# Revit family: GALAD Эконом GR LED
name_source: partatom
category: Осветительные приборы
revit_build: Autodesk Revit 2018 (Build: 20180423_1000(x64)
units: mm (PartAtom-declared; Revit-internal decimal feet)

## family parameters
Источник света = Да
Общий = Нет
Основа = Грань
При загрузке вырезать с полостями = Да
Размер круглого соединителя = Использовать диаметр
Тип детали = Нормальный
Точка расчета площади = Нет

## types (1)
- GALAD Эконом LED-35/У/П/4000/6060 GR
    ADSK_Версия Revit = 2018
    ADSK_Версия семейства = 1.01
    ADSK_Единица измерения = шт.
    ADSK_Завод-изготовитель = АО «КАДОШКИНСКИЙ ЭЛЕКТРОТЕХНИЧЕСКИЙ ЗАВОД»
    ADSK_Классификация нагрузок = Освещение
    ADSK_Код изделия = 17877
    ADSK_Количество = 1
    ADSK_Количество фаз = 1
    ADSK_Количество фаз числовое = 1
    ADSK_Коэффициент мощности = 0.95
    ADSK_Марка = GALAD Эконом LED-35/У/П/4000/6060 GR
    ADSK_Масса = 3.4
    ADSK_Наименование = GALAD Эконом LED-35/У/П/4000/6060 GR
    ADSK_Наименование краткое = GALAD Эконом LED-35/У/П/4000/6060 GR
    ADSK_Напряжение = 230 В
    ADSK_Номинальная мощность = 35 Вт
    ADSK_Обозначение = ГОСТ 15150-69
    ADSK_Полная мощность = 37 В·А
    ADSK_Размер_Высота = 45 мм
    ADSK_Размер_Длина = 588 мм
    ADSK_Размер_Ширина = 588 мм
    ADSK_Ток = 0 А
    ADSK_Энергоэффективность = 103 лм/Вт
    IP = 20
    URL = https://galad.ru
    Блок аварийного питания = Нет
    Бортик внешней рамки = 0 мм
    Видимая форма излучения при визуализации = Нет
    Возможный угол наклона = 0
    Высота бортика внешнего = 4 мм
    Габаритная яркость в зоне ограничения яркости = 0
    Группа модели = GALAD Эконом LED
    Диапазон цветовой температуры = 3985±275
    Излучение по длине прямоугольника = 588 мм
    Излучение по ширине прямоугольника = 588 мм
    Класс защиты от поражения электрическим током = 1
    Класс светораспределения = П
    Климатическая зона = УХЛ4
    Климатическое исполнение = 1…35 °С
    Корпус = Сталь
    Коэффициент пульсации = менее 5%
    Неравномерность яркости  = 0
    Область использования = офисное
    Описание = GALAD Эконом LED - это отличное решение для потребителей, чей бюджет ограничен, однако есть желание получить стабильно высокое качество. В Экономе используются 1-ваттные светодиоды.
    Отметка по умолчанию = 0 мм
    Плафон = ПММА
    Полная установленная мощность = 37 В·А
    Размер бортика видимого = 12 мм
    Рассеиватель = ПММА
    Самосвечение = Плафон самосвечение
    Световая отдача = 103
    Светофильтр = 16777215
    Смещение цветовой температуры при затухании лампы = <Нет>
    Снижение светового потока во время разгорания = не более 6%
    Срок службы = 12 лет
    Тип КСС = Косинусная
    Тип ПРА = ЭПРА
    Тип источника света = LED
    Тип монтажной поверхности = потолочный
    Тип продукции = светильник
    Тип устройства управления светодиодами = без управления
    УОИС = УОИС : Светильник светодиодный
    Угол наклона = -90.00°
    Файл фотометрической сетки = GALAD ekonom LED-35_u_p_4000_6060 GR.IES
    Цветопередача = 80
    Частота = 50
